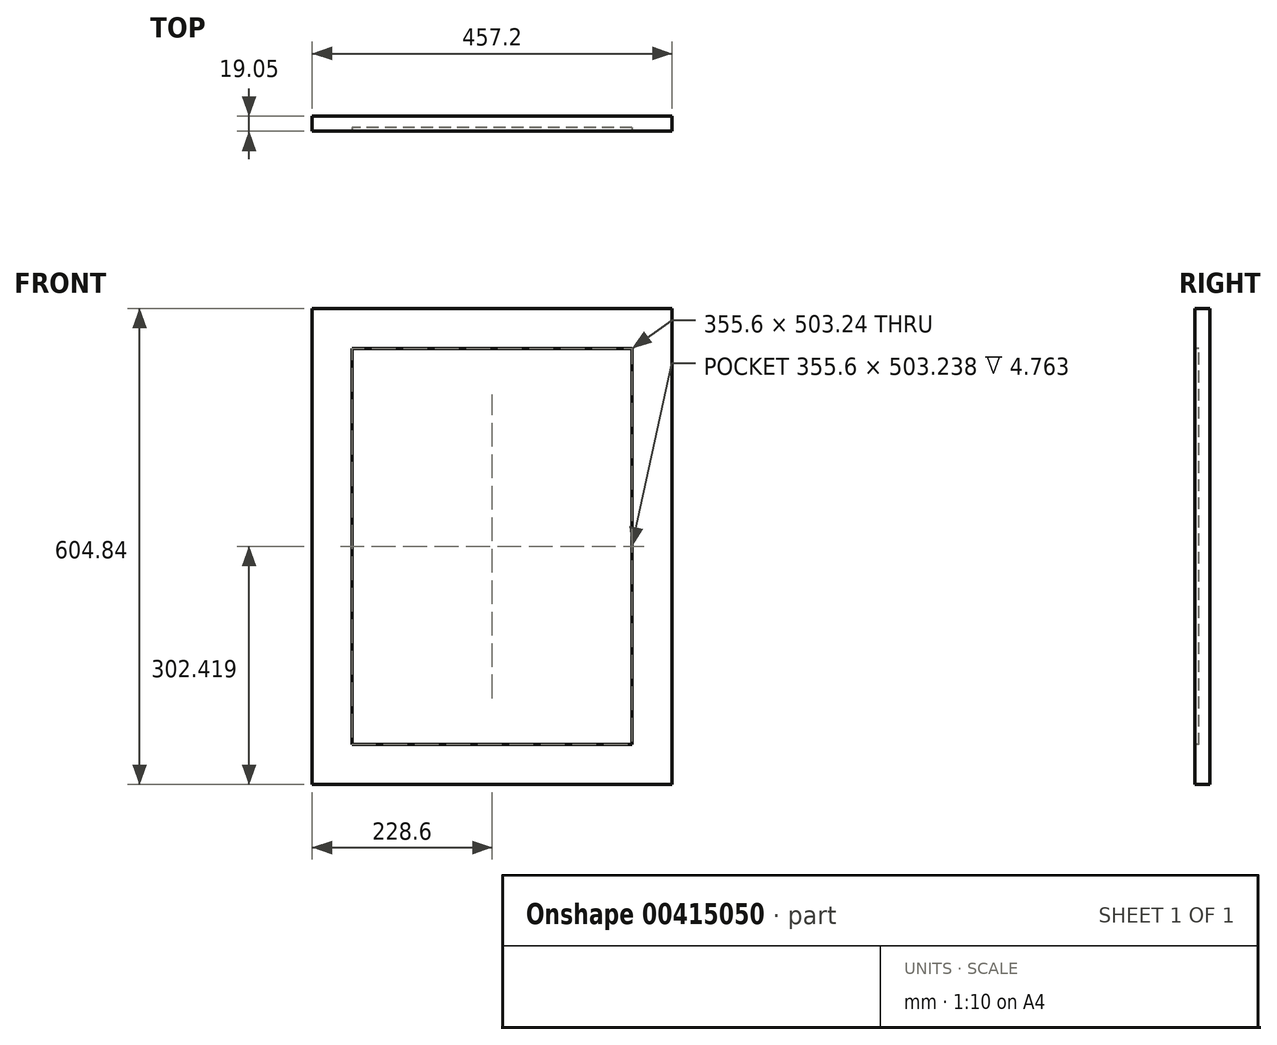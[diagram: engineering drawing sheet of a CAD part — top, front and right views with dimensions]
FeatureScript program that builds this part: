
annotation { "Feature Type Name" : "Feature", "Feature Type Description" : "" }
export const myFeature = defineFeature(function(context is Context, id is Id, definition is map)
    precondition{}
    {
        {
            var Q0;
            Q0=qCreatedBy(makeId("Front.planeOp"),FACE);
            var sketch = newSketch(context, id + "F0", { "sketchPlane" : qUnion([Q0])});
            skLineSegment(sketch, "E0.bottom", {"start": v(0, 0) * mm, "end": v(457.2, 0) * mm});
            skLineSegment(sketch, "E0.top", {"start": v(0, 604.84) * mm, "end": v(457.2, 604.84) * mm});
            skLineSegment(sketch, "E0.left", {"start": v(0, 0) * mm, "end": v(0, 604.84) * mm});
            skLineSegment(sketch, "E0.right", {"start": v(457.2, 0) * mm, "end": v(457.2, 604.84) * mm});
            skSolve(sketch);
        }
        {
            var Q0;
            Q0=makeQuery(id+"F0.imprint","IMPRINT",FACE,{"disambiguationData":[TD([[makeQuery(id+"F0.imprint","IMPRINT",EDGE,{"derivedFrom":sQuery(id+"F0.wireOp",EDGE,"E0.bottom")}),1.0]])]});
            extrude(context, id + "F1", {"entities" : qUnion([Q0]), "depth" : 19.05 * mm, "offsetDistance" : 25.4 * mm});
        }
        {
            var Q0;
            Q0=makeQuery(id+"F1.opExtrude","CAP_FACE",FACE,{"disambiguationData":[OSD([sQuery(id+"F0.wireOp",EDGE,"E0.bottom"),sQuery(id+"F0.wireOp",EDGE,"E0.top"),sQuery(id+"F0.wireOp",EDGE,"E0.left"),sQuery(id+"F0.wireOp",EDGE,"E0.right")])],"isStart":false});
            var sketch = newSketch(context, id + "F2", { "sketchPlane" : qUnion([Q0])});
            skLineSegment(sketch, "E1.0", {"start": v(406.4, 554.04) * mm, "end": v(50.8, 554.04) * mm});
            skLineSegment(sketch, "E1.1", {"start": v(406.4, 50.8) * mm, "end": v(406.4, 554.04) * mm});
            skLineSegment(sketch, "E1.2", {"start": v(50.8, 50.8) * mm, "end": v(406.4, 50.8) * mm});
            skLineSegment(sketch, "E1.3", {"start": v(50.8, 554.04) * mm, "end": v(50.8, 50.8) * mm});
            skSolve(sketch);
        }
        {
            var Q0;
            Q0=makeQuery(id+"F2.imprint","IMPRINT",FACE,{"disambiguationData":[TD([[makeQuery(id+"F2.imprint","IMPRINT",EDGE,{"derivedFrom":sQuery(id+"F2.wireOp",EDGE,"E1.0")}),1.0]])]});
            extrude(context, id + "F3", {"entities" : qUnion([Q0]), "operationType" : NewBodyOperationType.REMOVE, "oppositeDirection" : true, "depth" : 4.76 * mm, "offsetDistance" : 25.4 * mm});
        }
    });
